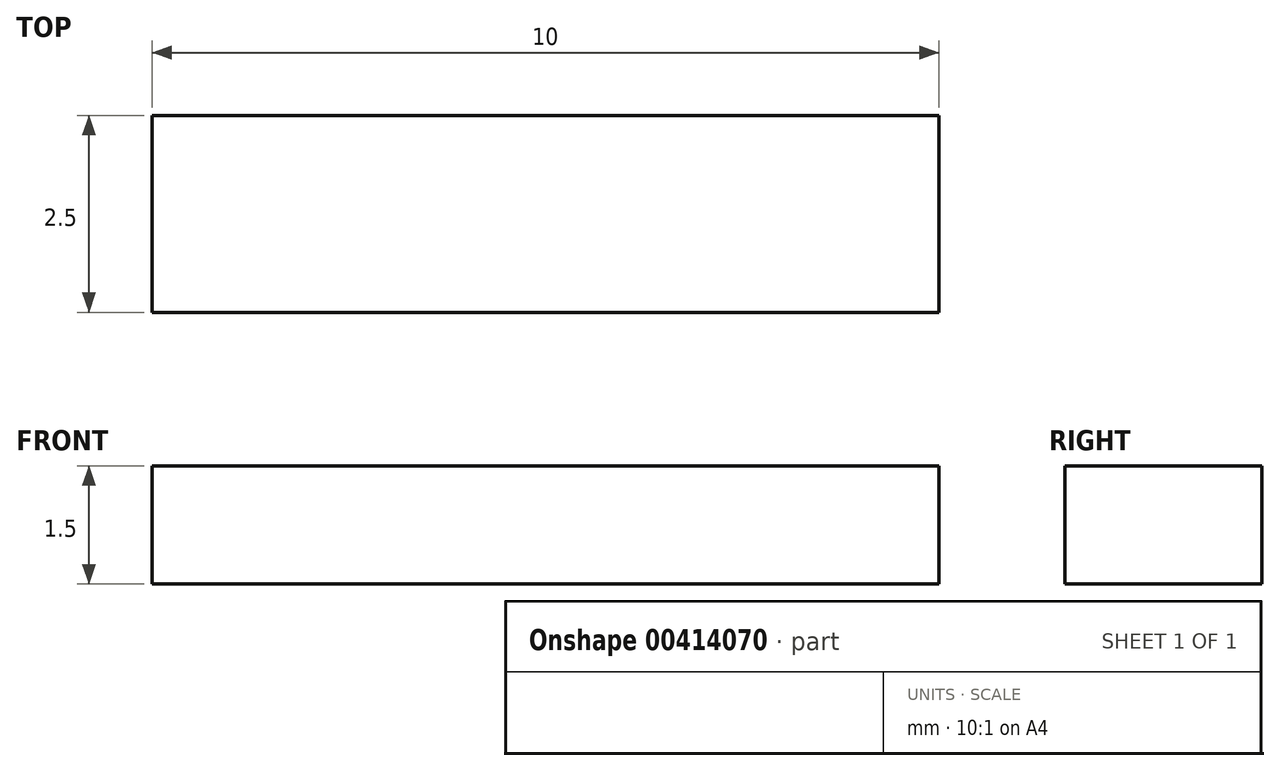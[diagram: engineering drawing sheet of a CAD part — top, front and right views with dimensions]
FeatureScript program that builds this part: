
annotation { "Feature Type Name" : "Feature", "Feature Type Description" : "" }
export const myFeature = defineFeature(function(context is Context, id is Id, definition is map)
    precondition{}
    {
        {
            var Q0;
            Q0=qCreatedBy(makeId("Front.planeOp"),FACE);
            var sketch = newSketch(context, id + "F0", { "sketchPlane" : qUnion([Q0])});
            skLineSegment(sketch, "E0.bottom", {"start": v(0, 0) * mm, "end": v(10, 0) * mm});
            skLineSegment(sketch, "E0.top", {"start": v(0, 1.5) * mm, "end": v(10, 1.5) * mm});
            skLineSegment(sketch, "E0.left", {"start": v(0, 0) * mm, "end": v(0, 1.5) * mm});
            skLineSegment(sketch, "E0.right", {"start": v(10, 0) * mm, "end": v(10, 1.5) * mm});
            skSolve(sketch);
        }
        {
            var Q0;
            Q0=makeQuery(id+"F0.imprint","IMPRINT",FACE,{"disambiguationData":[TD([[makeQuery(id+"F0.imprint","IMPRINT",EDGE,{"derivedFrom":sQuery(id+"F0.wireOp",EDGE,"E0.bottom")}),1.0]])]});
            extrude(context, id + "F1", {"entities" : qUnion([Q0]), "depth" : 2.5 * mm});
        }
    });
